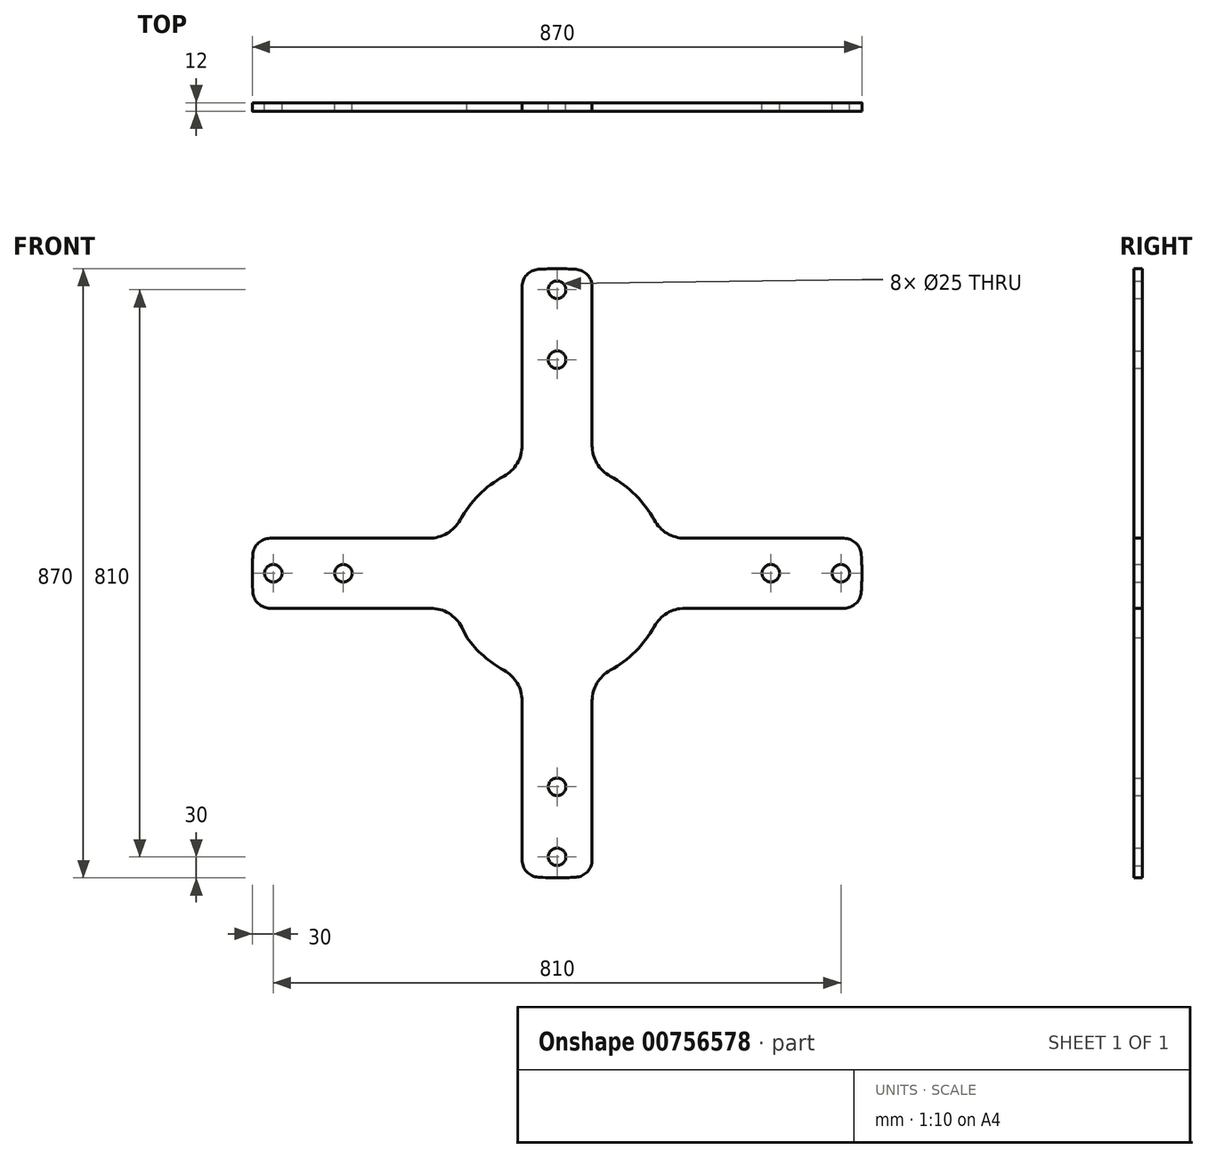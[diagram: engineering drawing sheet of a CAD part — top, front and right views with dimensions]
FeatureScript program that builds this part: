
annotation { "Feature Type Name" : "Feature", "Feature Type Description" : "" }
export const myFeature = defineFeature(function(context is Context, id is Id, definition is map)
    precondition{}
    {
        {
            var Q0;
            Q0=qCreatedBy(makeId("Front.planeOp"),FACE);
            var sketch = newSketch(context, id + "F0", { "sketchPlane" : qUnion([Q0])});
            skArc(sketch, "E0", {"start": v(26.52, 434.2) * mm, "mid": v(0, 435) * mm, "end": v(-26.52, 434.2) * mm});
            skLineSegment(sketch, "E1.0", {"start": v(-409.24, -50) * mm, "end": v(-209.94, -50) * mm});
            skLineSegment(sketch, "E2.0", {"start": v(-50, 409.24) * mm, "end": v(-50, 182.4) * mm});
            skLineSegment(sketch, "E3.0", {"start": v(50, 409.24) * mm, "end": v(50, 182.4) * mm});
            skLineSegment(sketch, "E4.0", {"start": v(-409.24, 50) * mm, "end": v(-182.4, 50) * mm});
            skLineSegment(sketch, "E5.trimOffspring", {"start": v(50, -182.4) * mm, "end": v(50, -409.24) * mm});
            skLineSegment(sketch, "E6.trimOffspring", {"start": v(-50, -182.4) * mm, "end": v(-50, -409.24) * mm});
            skLineSegment(sketch, "E7.trimOffspring", {"start": v(182.4, -50) * mm, "end": v(409.24, -50) * mm});
            skLineSegment(sketch, "E8.trimOffspring", {"start": v(182.4, 50) * mm, "end": v(409.24, 50) * mm});
            skCircle(sketch, "E9", {"center": v(0, 405) * mm, "radius": 12.5 * mm});
            skCircle(sketch, "E10", {"center": v(0, 305) * mm, "radius": 12.5 * mm});
            skPoint(sketch, "E11.visualSharp", {"position": v(50, 50) * mm});
            skArc(sketch, "E11.filletArc", {"start": v(50, 150) * mm, "mid": v(50, 149.95) * mm, "end": v(50, 149.9) * mm});
            skPoint(sketch, "E12.visualSharp", {"position": v(-50, 50) * mm});
            skArc(sketch, "E12.filletArc", {"start": v(-150, 50) * mm, "mid": v(-149.95, 50) * mm, "end": v(-149.9, 50) * mm});
            skPoint(sketch, "E13.visualSharp", {"position": v(-50, -50) * mm});
            skArc(sketch, "E13.filletArc", {"start": v(-50, -150) * mm, "mid": v(-50, -149.95) * mm, "end": v(-50, -149.9) * mm});
            skPoint(sketch, "E14.visualSharp", {"position": v(50, -50) * mm});
            skArc(sketch, "E14.filletArc", {"start": v(150, -50) * mm, "mid": v(149.95, -50) * mm, "end": v(149.9, -50) * mm});
            skCircle(sketch, "E15.1.0", {"center": v(-405, 0) * mm, "radius": 12.5 * mm});
            skCircle(sketch, "E15.1.1", {"center": v(-305, 0) * mm, "radius": 12.5 * mm});
            skCircle(sketch, "E15.2.0", {"center": v(0, -405) * mm, "radius": 12.5 * mm});
            skCircle(sketch, "E15.2.1", {"center": v(0, -305) * mm, "radius": 12.5 * mm});
            skCircle(sketch, "E15.3.0", {"center": v(405, 0) * mm, "radius": 12.5 * mm});
            skCircle(sketch, "E15.3.1", {"center": v(305, 0) * mm, "radius": 12.5 * mm});
            skArc(sketch, "E16.trimOffspring", {"start": v(-434.2, 26.52) * mm, "mid": v(-435, 0) * mm, "end": v(-434.2, -26.52) * mm});
            skArc(sketch, "E17.trimOffspring", {"start": v(-26.52, -434.2) * mm, "mid": v(0, -435) * mm, "end": v(26.52, -434.2) * mm});
            skArc(sketch, "E18.trimOffspring", {"start": v(434.2, -26.52) * mm, "mid": v(435, 0) * mm, "end": v(434.2, 26.52) * mm});
            skArc(sketch, "E19", {"start": v(-128.57, -91.86) * mm, "mid": v(-104.9, -118.18) * mm, "end": v(-75.96, -138.56) * mm});
            skArc(sketch, "E20.trimOffspring", {"start": v(50, -149.9) * mm, "mid": v(50, -149.95) * mm, "end": v(50, -150) * mm});
            skArc(sketch, "E21.trimOffspring", {"start": v(149.9, 50) * mm, "mid": v(149.95, 50) * mm, "end": v(150, 50) * mm});
            skArc(sketch, "E22.trimOffspring", {"start": v(-50, 149.9) * mm, "mid": v(-50, 149.95) * mm, "end": v(-50, 150) * mm});
            skArc(sketch, "E23.trimOffspring", {"start": v(-149.9, -50) * mm, "mid": v(-149.95, -50) * mm, "end": v(-150, -50) * mm});
            skArc(sketch, "E24.trimOffspring", {"start": v(-75.96, 138.56) * mm, "mid": v(-111.74, 111.74) * mm, "end": v(-138.56, 75.96) * mm});
            skArc(sketch, "E25.trimOffspring", {"start": v(138.56, 75.96) * mm, "mid": v(111.74, 111.74) * mm, "end": v(75.96, 138.56) * mm});
            skArc(sketch, "E26.trimOffspring", {"start": v(75.96, -138.56) * mm, "mid": v(111.74, -111.74) * mm, "end": v(138.56, -75.96) * mm});
            skArc(sketch, "E27.filletArc", {"start": v(-50, -182.4) * mm, "mid": v(-56.98, -156.93) * mm, "end": v(-75.96, -138.56) * mm});
            skArc(sketch, "E28.filletArc", {"start": v(75.96, -138.56) * mm, "mid": v(56.98, -156.93) * mm, "end": v(50, -182.4) * mm});
            skArc(sketch, "E29.filletArc", {"start": v(182.4, -50) * mm, "mid": v(156.93, -56.98) * mm, "end": v(138.56, -75.96) * mm});
            skArc(sketch, "E30.filletArc", {"start": v(138.56, 75.96) * mm, "mid": v(156.93, 56.98) * mm, "end": v(182.4, 50) * mm});
            skArc(sketch, "E31.filletArc", {"start": v(50, 182.4) * mm, "mid": v(56.98, 156.93) * mm, "end": v(75.96, 138.56) * mm});
            skArc(sketch, "E32.filletArc", {"start": v(-75.96, 138.56) * mm, "mid": v(-56.98, 156.93) * mm, "end": v(-50, 182.4) * mm});
            skArc(sketch, "E33.filletArc", {"start": v(-182.4, 50) * mm, "mid": v(-156.93, 56.98) * mm, "end": v(-138.56, 75.96) * mm});
            skLineSegment(sketch, "E34", {"start": v(-209.94, -50) * mm, "end": v(-180.54, -50) * mm});
            skLineSegment(sketch, "E35", {"start": v(-136, -77.3) * mm, "end": v(-128.57, -91.86) * mm});
            skPoint(sketch, "E36.visualSharp", {"position": v(-149.9, -50) * mm});
            skArc(sketch, "E36.filletArc", {"start": v(-136, -77.3) * mm, "mid": v(-154.42, -57.37) * mm, "end": v(-180.54, -50) * mm});
            skPoint(sketch, "E37.visualSharp", {"position": v(-432.12, 50) * mm});
            skArc(sketch, "E37.filletArc", {"start": v(-409.24, 50) * mm, "mid": v(-426.37, 43.2) * mm, "end": v(-434.2, 26.52) * mm});
            skPoint(sketch, "E38.visualSharp", {"position": v(-432.12, -50) * mm});
            skArc(sketch, "E38.filletArc", {"start": v(-434.2, -26.52) * mm, "mid": v(-426.37, -43.2) * mm, "end": v(-409.24, -50) * mm});
            skPoint(sketch, "E39.visualSharp", {"position": v(-50, -432.12) * mm});
            skArc(sketch, "E39.filletArc", {"start": v(-50, -409.24) * mm, "mid": v(-43.2, -426.37) * mm, "end": v(-26.52, -434.2) * mm});
            skPoint(sketch, "E40.visualSharp", {"position": v(50, -432.12) * mm});
            skArc(sketch, "E40.filletArc", {"start": v(26.52, -434.2) * mm, "mid": v(43.2, -426.37) * mm, "end": v(50, -409.24) * mm});
            skPoint(sketch, "E41.visualSharp", {"position": v(432.12, 50) * mm});
            skArc(sketch, "E41.filletArc", {"start": v(434.2, 26.52) * mm, "mid": v(426.37, 43.2) * mm, "end": v(409.24, 50) * mm});
            skPoint(sketch, "E42.visualSharp", {"position": v(432.12, -50) * mm});
            skArc(sketch, "E42.filletArc", {"start": v(409.24, -50) * mm, "mid": v(426.37, -43.2) * mm, "end": v(434.2, -26.52) * mm});
            skPoint(sketch, "E43.visualSharp", {"position": v(-50, 432.12) * mm});
            skArc(sketch, "E43.filletArc", {"start": v(-26.52, 434.2) * mm, "mid": v(-43.2, 426.37) * mm, "end": v(-50, 409.24) * mm});
            skPoint(sketch, "E44.visualSharp", {"position": v(50, 432.12) * mm});
            skArc(sketch, "E44.filletArc", {"start": v(50, 409.24) * mm, "mid": v(43.2, 426.37) * mm, "end": v(26.52, 434.2) * mm});
            skSolve(sketch);
        }
        {
            var Q0;
            Q0=makeQuery(id+"F0.imprint","IMPRINT",FACE,{"disambiguationData":[TD([[makeQuery(id+"F0.imprint","IMPRINT",EDGE,{"derivedFrom":sQuery(id+"F0.wireOp",EDGE,"E0")}),1.0]])]});
            extrude(context, id + "F1", {"entities" : qUnion([Q0]), "depth" : 12 * mm, "offsetDistance" : 25 * mm});
        }
    });
